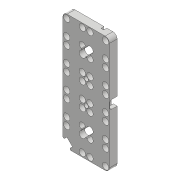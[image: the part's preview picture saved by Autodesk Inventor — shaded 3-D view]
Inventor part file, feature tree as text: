
AUTODESK INVENTOR PART (.ipt)
format: ipt  version: 2018 (Build 220112000, 112)  size: 1,080,832 bytes
history: native  units: mm
features: projected_geometry x15, extrude x13, sketch x12, fillet x7, pattern_linear x6, mirror x1
ambient origin geometry x8: Origin, YZ Plane, XZ Plane, XY Plane, X Axis, Y Axis, Z Axis, Center Point
bodies: Solid1 (feature_tree)
feature tree (54):
  extrude  "Extrusion1"  Depth=44.0mm
  extrude  "Extrusion2"  Depth=22.0mm
  extrude  "Extrusion3"  Depth=22.0mm
  pattern_linear  "Rectangular Pattern1"  Count1=5 Spacing1=22.0mm
  extrude  "Extrusion4"  Depth=10.0mm
  pattern_linear  "Rectangular Pattern2"  Spacing1=5.0mm  [1 undecoded]
  extrude  "Extrusion5"  Depth=5.0mm
  pattern_linear  "Rectangular Pattern3"  Spacing1=2.0mm  [1 undecoded]
  fillet  "Fillet1"  Radius=50.0mm
  extrude  "Extrusion6"  Depth=2.0mm TaperAngle=0.0deg
  extrude  "Extrusion9"  Depth=22.0mm
  pattern_linear  "Rectangular Pattern4"  Spacing1=1.0mm  [1 undecoded]
  extrude  "Extrusion7"  Depth=1.0mm
  pattern_linear  "Rectangular Pattern5"  Spacing1=6.7mm  [1 undecoded]
  pattern_linear  "Rectangular Pattern6"  Count1=2 Spacing1=66.0mm
  fillet  "Fillet2"  Radius=4.0mm
  fillet  "Fillet3"  Radius=2.0mm
  fillet  "Fillet4"  Radius=22.0mm
  extrude  "Extrusion8"  Depth=4.0mm
  fillet  "Fillet5"  Radius=0.5mm
  extrude  "Extrusion10"  Depth=1.0mm
  extrude  "Extrusion11"  Depth=2.5mm
  fillet  "Fillet6"  Radius=3.0mm
  extrude  "Extrusion12"  Depth=0.5mm
  extrude  "Extrusion13"  Depth=2.0mm
  fillet  "Fillet7"  Radius=2.0mm
  mirror  "Mirror1"
  sketch  "Sketch1"  dims[d0=110.0mm d1=44.0mm]
  sketch  "Sketch2"  dims[d2=7.3mm d3=0.0mm d4=22.0mm]
  projected_geometry  "Projected Loop1"
  sketch  "Sketch3"  dims[d5=22.0mm d6=14.75mm]
  projected_geometry  "Projected Loop2"
  projected_geometry  "Projected Loop3"
  projected_geometry  "Projected Loop4"
  projected_geometry  "Projected Loop5"
  sketch  "Sketch4"  dims[d7=7.5mm]
  projected_geometry  "Projected Loop6"
  sketch  "Sketch5"  dims[d8=7.0mm d9=0.0mm]
  projected_geometry  "Projected Loop7"
  projected_geometry  "Projected Loop8"
  sketch  "Sketch7"  dims[d10=6.7mm d11=0.0mm]
  projected_geometry  "Projected Loop9"
  sketch  "Sketch8"  dims[d12=6.0mm]
  projected_geometry  "Projected Loop10"
  sketch  "Sketch9"  dims[d13=6.0mm]
  sketch  "Sketch10"  dims[d14=6.0mm]
  sketch  "Sketch11"  dims[d15=6.0mm d16=50.0mm d18=22.0mm]
  projected_geometry  "Projected Loop11"
  projected_geometry  "Projected Loop12"
  projected_geometry  "Projected Loop13"
  sketch  "Sketch12"  dims[d19=20.0mm d21=22.0mm d22=10.0mm]
  projected_geometry  "Projected Loop14"
  sketch  "Sketch13"  dims[d23=5.0mm d24=5.0mm d25=5.0mm d26=2.0mm d27=0.0mm d28=50.0mm d30=22.0mm d31=2.0mm d32=0.0mm d33=20.0mm d35=22.0mm d36=1.0mm d37=8.5mm d38=6.7mm d39=0.0mm d40=20.0mm d42=66.0mm d43=4.0mm d44=2.0mm d45=0.0mm d46=20.0mm d48=22.0mm d49=4.0mm d50=0.5mm d51=1.0mm d52=2.5mm d53=3.0mm d54=0.0mm d55=0.5mm d56=2.0mm d57=2.0mm d58=2.0mm d59=2.0mm d60=2.0mm d61=2.0mm d62=2.0mm d63=2.0mm d64=10.0mm d65=0.0mm d66=40.0mm d68=22.0mm d69=8.0mm d70=10.0mm d71=0.0mm d72=10.0mm d73=0.0mm d74=2.0mm d75=45.0deg d76=18.0mm d77=7.5mm d78=10.0mm d79=0.0mm d80=4.0mm d81=12.0mm d82=0.0mm d83=0.0mm d84=1.0mm]
  projected_geometry  "Projected Loop15"
note: 4 required parameter values undecoded (feature->parameter linkage not recoverable at this tier; creation-order binding heuristic only, values carry confidence <= 0.55)
